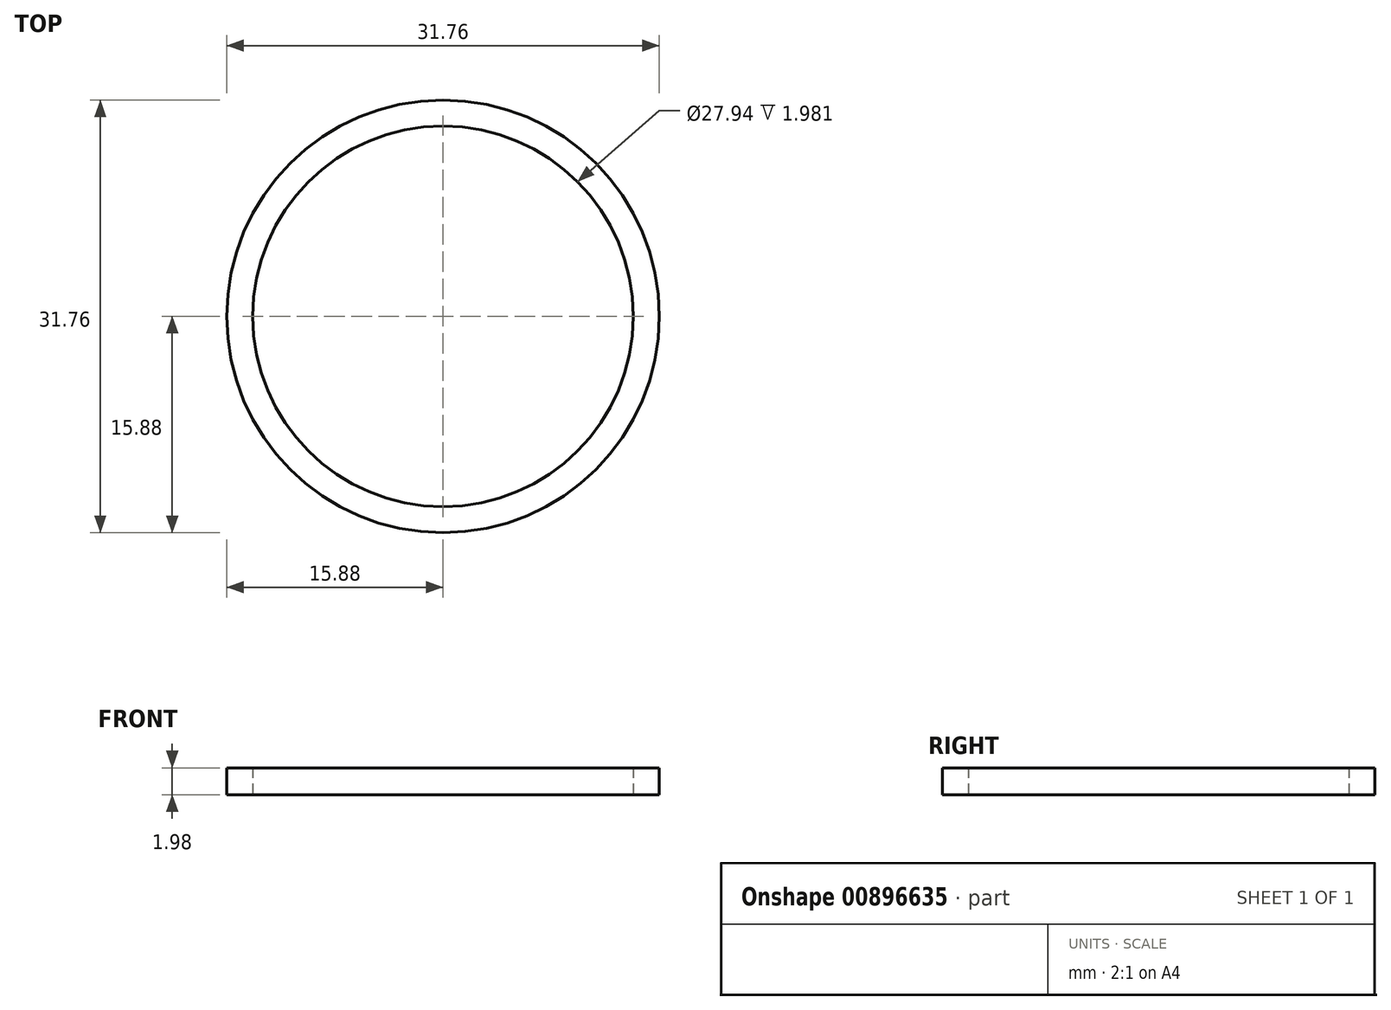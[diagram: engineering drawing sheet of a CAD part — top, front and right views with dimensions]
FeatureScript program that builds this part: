
annotation { "Feature Type Name" : "Feature", "Feature Type Description" : "" }
export const myFeature = defineFeature(function(context is Context, id is Id, definition is map)
    precondition{}
    {
        {
            var Q0;
            Q0=qCreatedBy(makeId("Top.planeOp"),FACE);
            var sketch = newSketch(context, id + "F0", { "sketchPlane" : qUnion([Q0])});
            skCircle(sketch, "E0", {"center": v(0, 0) * mm, "radius": 15.88 * mm});
            skCircle(sketch, "E1", {"center": v(0, 0) * mm, "radius": 13.97 * mm});
            skSolve(sketch);
        }
        {
            var Q0;
            Q0=makeQuery(id+"F0.imprint","IMPRINT",FACE,{"disambiguationData":[TD([[makeQuery(id+"F0.imprint","IMPRINT",EDGE,{"derivedFrom":sQuery(id+"F0.wireOp",EDGE,"E0")}),-1.0]])]});
            var Q1;
            Q1=makeQuery(id+"F0.imprint","IMPRINT",FACE,{"disambiguationData":[TD([[makeQuery(id+"F0.imprint","IMPRINT",EDGE,{"derivedFrom":sQuery(id+"F0.wireOp",EDGE,"E0")}),1.0]])]});
            extrude(context, id + "F1", {"entities" : qUnion([Q0, Q1]), "depth" : 1.98 * mm, "offsetDistance" : 25.4 * mm});
        }
    });
